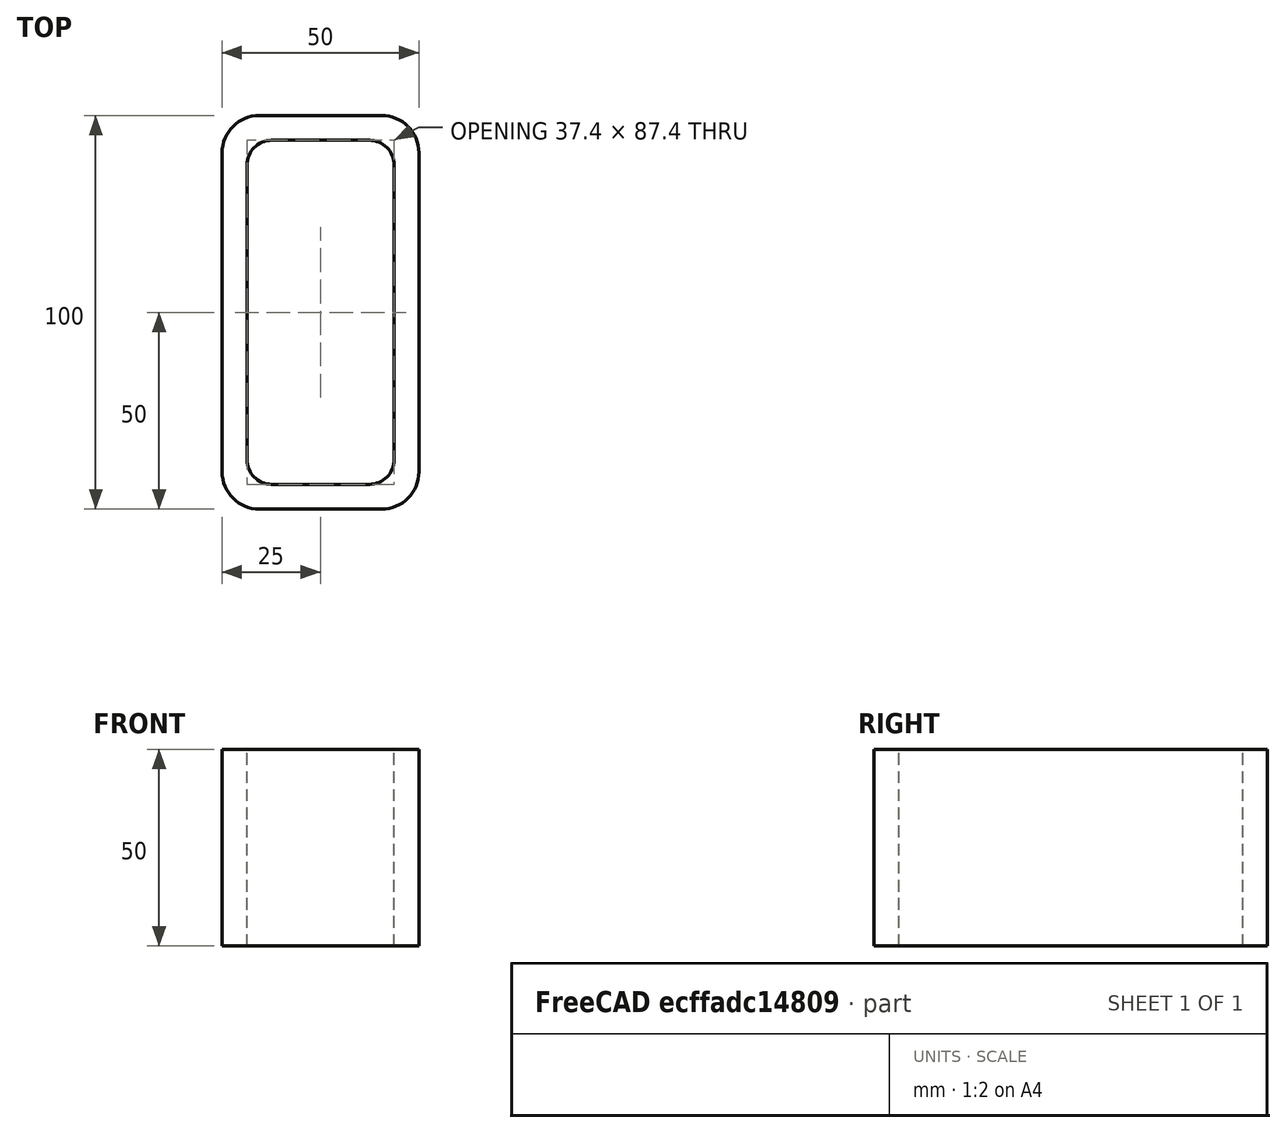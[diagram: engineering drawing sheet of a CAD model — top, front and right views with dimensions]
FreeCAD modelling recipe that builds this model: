
FCSTD DOCUMENT  (FreeCAD 0.15R4671 (Git))
Label: Rectangular hollow section 100x50x6.3 EN10219 S235JRH
License: All rights reserved
LicenseURL: http://en.wikipedia.org/wiki/All_rights_reserved
objects: Sketcher::SketchObject×1, Part::Extrusion×1
note: 2 computed .brp shape members not serialized (recipe doc carries the construction recipe); baked Part::Feature solids carry a one-line shape summary decoded from their .brp

FEATURE [Sketcher::SketchObject] Sketch
  sketch-geometry (16):
    g0: LineSegment StartX=-12.4 StartY=43.7 StartZ=0 EndX=12.4 EndY=43.7 EndZ=0
    g1: LineSegment StartX=18.7 StartY=37.4 StartZ=0 EndX=18.7 EndY=-37.4 EndZ=0
    g2: LineSegment StartX=12.4 StartY=-43.7 StartZ=0 EndX=-12.4 EndY=-43.7 EndZ=0
    g3: LineSegment StartX=-18.7 StartY=-37.4 StartZ=0 EndX=-18.7 EndY=37.4 EndZ=0
    g4: LineSegment StartX=-15.55 StartY=50 StartZ=0 EndX=15.55 EndY=50 EndZ=0
    g5: LineSegment StartX=25 StartY=40.55 StartZ=0 EndX=25 EndY=-40.55 EndZ=0
    g6: LineSegment StartX=15.55 StartY=-50 StartZ=0 EndX=-15.55 EndY=-50 EndZ=0
    g7: LineSegment StartX=-25 StartY=-40.55 StartZ=0 EndX=-25 EndY=40.55 EndZ=0
    g8: ArcOfCircle CenterX=-12.4 CenterY=37.4 CenterZ=0 NormalX=0 NormalY=0 NormalZ=1 Radius=6.3 StartAngle=1.5708 EndAngle=3.14159
    g9: ArcOfCircle CenterX=12.4 CenterY=37.4 CenterZ=0 NormalX=0 NormalY=0 NormalZ=1 Radius=6.3 StartAngle=0 EndAngle=1.5708
    g10: ArcOfCircle CenterX=12.4 CenterY=-37.4 CenterZ=0 NormalX=0 NormalY=0 NormalZ=1 Radius=6.3 StartAngle=4.71239 EndAngle=6.28319
    g11: ArcOfCircle CenterX=-12.4 CenterY=-37.4 CenterZ=0 NormalX=0 NormalY=0 NormalZ=1 Radius=6.3 StartAngle=3.14159 EndAngle=4.71239
    g12: ArcOfCircle CenterX=15.55 CenterY=40.55 CenterZ=0 NormalX=0 NormalY=0 NormalZ=1 Radius=9.45 StartAngle=0 EndAngle=1.5708
    g13: ArcOfCircle CenterX=15.55 CenterY=-40.55 CenterZ=0 NormalX=0 NormalY=0 NormalZ=1 Radius=9.45 StartAngle=4.71239 EndAngle=6.28319
    g14: ArcOfCircle CenterX=-15.55 CenterY=-40.55 CenterZ=0 NormalX=0 NormalY=0 NormalZ=1 Radius=9.45 StartAngle=3.14159 EndAngle=4.71239
    g15: ArcOfCircle CenterX=-15.55 CenterY=40.55 CenterZ=0 NormalX=0 NormalY=0 NormalZ=1 Radius=9.45 StartAngle=1.5708 EndAngle=3.14159
  constraints (36):
    c: Horizontal(g2)
    c: Vertical(g3)
    c: Horizontal(g6)
    c: Vertical(g7)
    c: Tangent(g3,g8) = 1.5708
    c: Tangent(g0,g8) = 1.5708
    c: Tangent(g0,g9) = 1.5708
    c: Tangent(g1,g9) = 1.5708
    c: Tangent(g1,g10) = 1.5708
    c: Tangent(g2,g10) = 1.5708
    c: Tangent(g2,g11) = 1.5708
    c: Tangent(g3,g11) = 1.5708
    c: Tangent(g4,g12) = 1.5708
    c: Tangent(g5,g12) = 1.5708
    c: Tangent(g5,g13) = 1.5708
    c: Tangent(g6,g13) = 1.5708
    c: Tangent(g6,g14) = 1.5708
    c: Tangent(g7,g14) = 1.5708
    c: Tangent(g7,g15) = 1.5708
    c: Tangent(g4,g15) = 1.5708
    c: Equal(g9,g8)
    c: Equal(g9,g11)
    c: Equal(g9,g10)
    c: Equal(g12,g15)
    c: Equal(g12,g14)
    c: Equal(g12,g13)
    c: Symmetric(g4,g6,g-1)
    c: Symmetric(g7,g5,g-2)
    c: DistanceY(g4,g6) = -100
    c: DistanceX(g7,g5) = 50
    c: Symmetric(g3,g1,g-2)
    c: Symmetric(g0,g2,g-1)
    c: DistanceY(g0,g4) = 6.3
    c: DistanceX(g5,g1) = -6.3
    c: Radius(g9) = 6.3
    c: Radius(g12) = 9.45
FEATURE [Part::Extrusion] Extrude  label="Rectangular hollow section 100x50x6.3 EN10219 S235JRH"
  Base = -> Sketch
  Dir = (0,0,50)
  Solid = true
